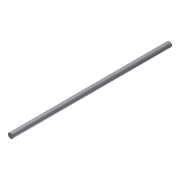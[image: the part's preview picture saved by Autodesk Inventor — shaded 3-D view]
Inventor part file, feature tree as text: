
AUTODESK INVENTOR PART (.ipt)
format: ipt  version: 2013 (Build 170138000, 138)  size: 81,408 bytes
history: native  units: in
note: dims shown in document units (in); Inventor stores cm internally (conversion verified against a paired STEP export)
features: other x1, imported_body x1, extrude x1, sketch x1
ambient origin geometry x8: Origin, YZ Plane, XZ Plane, XY Plane, X Axis, Y Axis, Z Axis, Center Point
feature tree (4):
  other  "AXLE_D-SHAFT_250_2011"
  imported_body  "Base1"
  extrude  "Extrusion1"  [1 undecoded]
  sketch  "Sketch1"  dims[d0=4.098in d1=0.0in]
note: 1 required parameter value undecoded (feature->parameter linkage not recoverable at this tier; creation-order binding heuristic only, values carry confidence <= 0.55)
